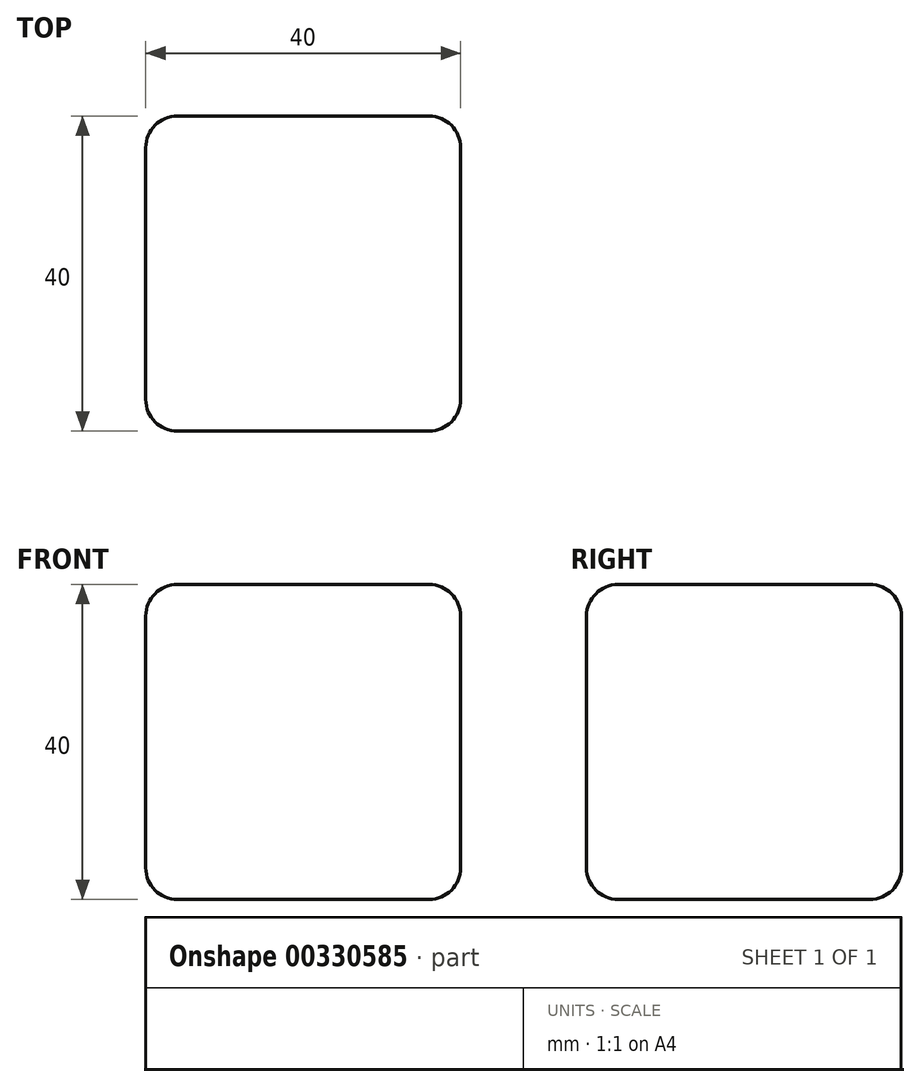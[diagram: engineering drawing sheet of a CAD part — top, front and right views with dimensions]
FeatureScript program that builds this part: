
annotation { "Feature Type Name" : "Feature", "Feature Type Description" : "" }
export const myFeature = defineFeature(function(context is Context, id is Id, definition is map)
    precondition{}
    {
        {
            var Q0;
            Q0=qCreatedBy(makeId("Right.planeOp"),FACE);
            var sketch = newSketch(context, id + "F0", { "sketchPlane" : qUnion([Q0])});
            skLineSegment(sketch, "E0.bottom", {"start": v(0, 0) * mm, "end": v(40, 0) * mm});
            skLineSegment(sketch, "E0.top", {"start": v(0, 40) * mm, "end": v(40, 40) * mm});
            skLineSegment(sketch, "E0.left", {"start": v(0, 0) * mm, "end": v(0, 40) * mm});
            skLineSegment(sketch, "E0.right", {"start": v(40, 0) * mm, "end": v(40, 40) * mm});
            skSolve(sketch);
        }
        {
            var Q0;
            Q0 = qSketchRegion(id + "F0", true);
            extrude(context, id + "F1", {"entities" : qUnion([Q0]), "depth" : 40 * mm});
        }
        {
            var Q0;
            Q0=makeQuery(id+"F1.opExtrude","CAP_EDGE",EDGE,{"disambiguationData":[OSD([sQuery(id+"F0.wireOp",EDGE,"E0.left")])],"isStart":true});
            var Q1;
            Q1=makeQuery(id+"F1.opExtrude","CAP_EDGE",EDGE,{"disambiguationData":[OSD([sQuery(id+"F0.wireOp",EDGE,"E0.top")])],"isStart":true});
            var Q2;
            Q2=makeQuery(id+"F1.opExtrude","SWEPT_EDGE",EDGE,{"disambiguationData":[OSD([sQuery(id+"F0.wireOp",EDGE,"E0.top"),sQuery(id+"F0.wireOp",EDGE,"E0.left")])]});
            var Q3;
            Q3=makeQuery(id+"F1.opExtrude","SWEPT_EDGE",EDGE,{"disambiguationData":[OSD([sQuery(id+"F0.wireOp",EDGE,"E0.bottom"),sQuery(id+"F0.wireOp",EDGE,"E0.left")])]});
            var Q4;
            Q4=makeQuery(id+"F1.opExtrude","CAP_EDGE",EDGE,{"disambiguationData":[OSD([sQuery(id+"F0.wireOp",EDGE,"E0.left")])],"isStart":false});
            var Q5;
            Q5=makeQuery(id+"F1.opExtrude","CAP_EDGE",EDGE,{"disambiguationData":[OSD([sQuery(id+"F0.wireOp",EDGE,"E0.bottom")])],"isStart":true});
            var Q6;
            Q6=makeQuery(id+"F1.opExtrude","CAP_EDGE",EDGE,{"disambiguationData":[OSD([sQuery(id+"F0.wireOp",EDGE,"E0.right")])],"isStart":true});
            var Q7;
            Q7=makeQuery(id+"F1.opExtrude","SWEPT_EDGE",EDGE,{"disambiguationData":[OSD([sQuery(id+"F0.wireOp",EDGE,"E0.top"),sQuery(id+"F0.wireOp",EDGE,"E0.right")])]});
            var Q8;
            Q8=makeQuery(id+"F1.opExtrude","CAP_EDGE",EDGE,{"disambiguationData":[OSD([sQuery(id+"F0.wireOp",EDGE,"E0.top")])],"isStart":false});
            var Q9;
            Q9=makeQuery(id+"F1.opExtrude","CAP_EDGE",EDGE,{"disambiguationData":[OSD([sQuery(id+"F0.wireOp",EDGE,"E0.bottom")])],"isStart":false});
            var Q10;
            Q10=makeQuery(id+"F1.opExtrude","SWEPT_EDGE",EDGE,{"disambiguationData":[OSD([sQuery(id+"F0.wireOp",EDGE,"E0.bottom"),sQuery(id+"F0.wireOp",EDGE,"E0.right")])]});
            var Q11;
            Q11=makeQuery(id+"F1.opExtrude","CAP_EDGE",EDGE,{"disambiguationData":[OSD([sQuery(id+"F0.wireOp",EDGE,"E0.right")])],"isStart":false});
            fillet(context, id + "F2", {"entities" : qUnion([Q0, Q1, Q2, Q3, Q4, Q5, Q6, Q7, Q8, Q9, Q10, Q11]), "radius" : 4 * mm, "tangentPropagation" : true, "allowEdgeOverflow" : false});
        }
    });
